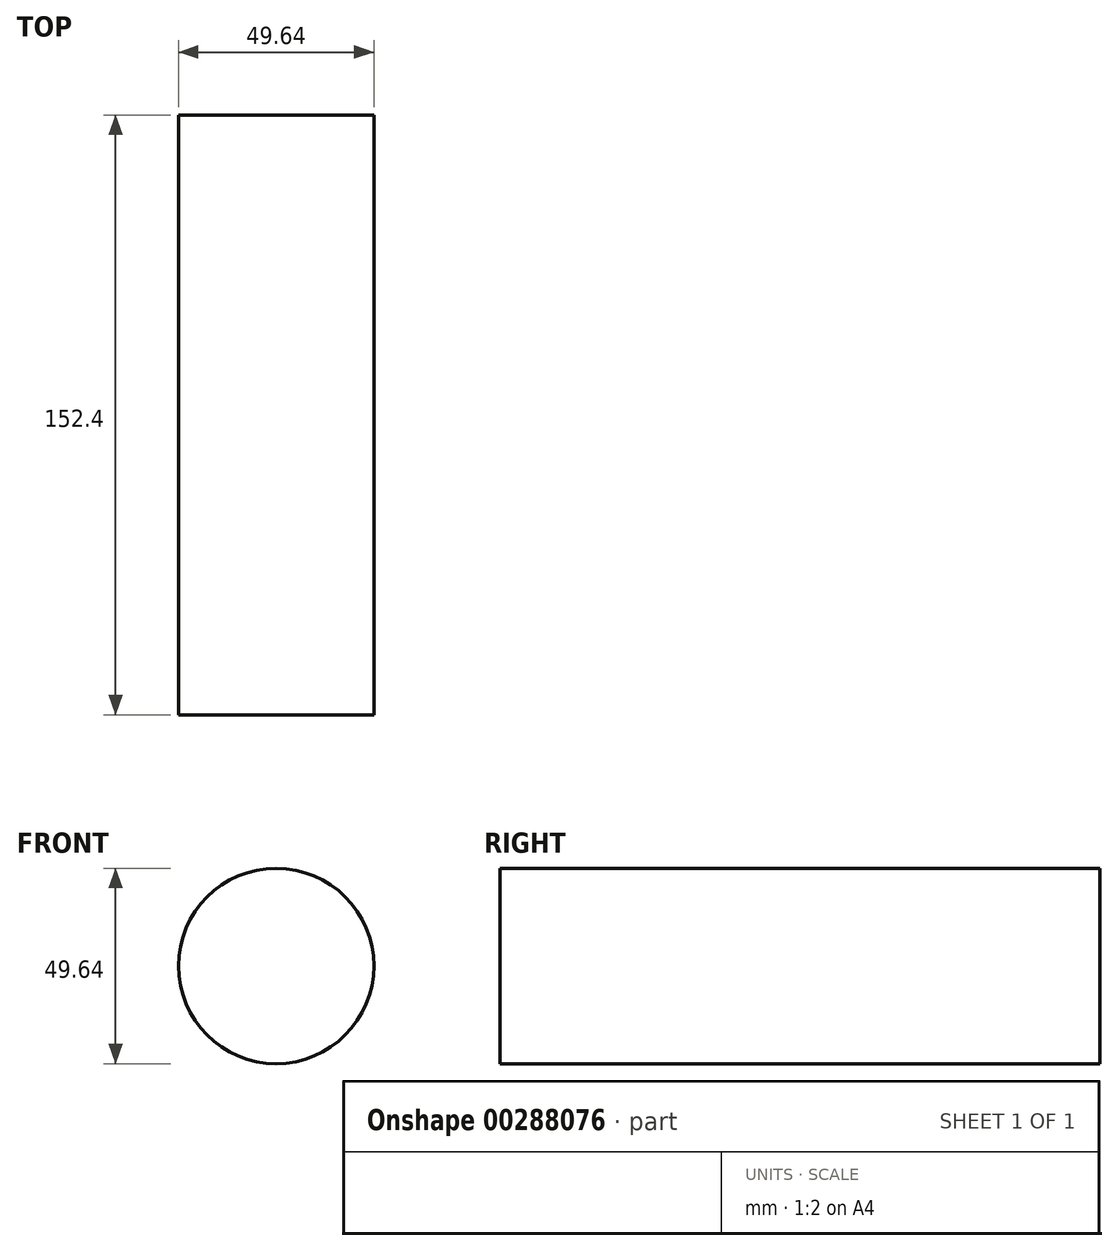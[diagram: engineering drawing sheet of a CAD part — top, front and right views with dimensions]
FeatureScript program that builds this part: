
annotation { "Feature Type Name" : "Feature", "Feature Type Description" : "" }
export const myFeature = defineFeature(function(context is Context, id is Id, definition is map)
    precondition{}
    {
        {
            var Q0;
            Q0=qCreatedBy(makeId("Front.planeOp"),FACE);
            var sketch = newSketch(context, id + "F0", { "sketchPlane" : qUnion([Q0])});
            skCircle(sketch, "E0", {"center": v(0, 0) * mm, "radius": 24.82 * mm});
            skSolve(sketch);
        }
        {
            var Q0;
            Q0=makeQuery(id+"F0.imprint","IMPRINT",FACE,{"disambiguationData":[TD([[makeQuery(id+"F0.imprint","IMPRINT",EDGE,{"derivedFrom":sQuery(id+"F0.wireOp",EDGE,"E0")}),1.0]])]});
            extrude(context, id + "F1", {"entities" : qUnion([Q0]), "depth" : 152.4 * mm});
        }
    });
